FCSTD DOCUMENT  (FreeCAD 1.1R39176 (Git))
Label: hackrf2
License: All rights reserved
LicenseURL: https://en.wikipedia.org/wiki/All_rights_reserved
objects: Sketcher::SketchObject×1, PartDesign::Body×1
note: 3 computed .brp shape members not serialized (recipe doc carries the construction recipe); baked Part::Feature solids carry a one-line shape summary decoded from their .brp

FEATURE [Sketcher::SketchObject] Sketch
  ArcFitTolerance = 1e-06
  AttachmentSupport = -> [XY_Plane]
  FullyConstrained = false
  MakeInternals = false
  MapMode = 5
  sketch-geometry (26):
    g0: Circle CenterX=-8.35591 CenterY=25.54 CenterZ=0 NormalX=0 NormalY=0 NormalZ=1 AngleXU=0 Radius=1.65
    g1: Circle CenterX=58.7441 CenterY=25.54 CenterZ=0 NormalX=0 NormalY=0 NormalZ=1 AngleXU=0 Radius=1.65
    g2: LineSegment [constr] StartX=-92.1126 StartY=25.54 StartZ=0 EndX=115.727 EndY=25.54 EndZ=0
    g3: GeomPoint [constr] X=-10.0059 Y=25.54 Z=0
    g4: GeomPoint [constr] X=60.3941 Y=25.54 Z=0
    g5: Circle CenterX=19.1744 CenterY=-19.1627 CenterZ=0 NormalX=0 NormalY=0 NormalZ=1 AngleXU=0 Radius=1.65
    g6: Circle CenterX=58.7441 CenterY=-30.3 CenterZ=0 NormalX=0 NormalY=0 NormalZ=1 AngleXU=0 Radius=1.65
    g7: Circle CenterX=58.7441 CenterY=-92.13 CenterZ=0 NormalX=0 NormalY=0 NormalZ=1 AngleXU=0 Radius=1.65
    g8: Circle CenterX=55.1135 CenterY=37.367 CenterZ=0 NormalX=0 NormalY=0 NormalZ=1 AngleXU=0 Radius=1.65
    g9: Circle CenterX=-8.35591 CenterY=-92.13 CenterZ=0 NormalX=0 NormalY=0 NormalZ=1 AngleXU=0 Radius=1.65
    g10: GeomPoint [constr] X=-9.22115 Y=26.945 Z=0
    g11: GeomPoint [constr] X=20.0397 Y=-20.5676 Z=0
    g12: LineSegment [constr] StartX=-21.7434 StartY=47.2782 StartZ=0 EndX=29.3252 EndY=-35.645 EndZ=0
    g13: GeomPoint [constr] X=18.0808 Y=-20.3982 Z=0
    g14: LineSegment [constr] StartX=44.9983 StartY=10.0112 StartZ=0 EndX=-3.8972 EndY=-45.2271 EndZ=0
    g15: GeomPoint [constr] X=59.8377 Y=26.7755 Z=0
    g16: LineSegment [constr] StartX=58.7441 StartY=53.8008 StartZ=0 EndX=58.7441 EndY=-140.054 EndZ=0
    g17: GeomPoint [constr] X=58.7441 Y=23.89 Z=0
    g18: GeomPoint [constr] X=58.7441 Y=-28.65 Z=0
    g19: GeomPoint [constr] X=58.7441 Y=-93.78 Z=0
    g20: GeomPoint [constr] X=58.7441 Y=-28.65 Z=0
    g21: LineSegment [constr] StartX=131.191 StartY=-92.13 StartZ=0 EndX=-53.1494 EndY=-92.13 EndZ=0
    g22: LineSegment [constr] StartX=-8.35591 StartY=91.9074 StartZ=0 EndX=-8.35591 EndY=-151.657 EndZ=0
    g23: LineSegment [constr] StartX=-28.9239 StartY=-5.62487 StartZ=0 EndX=81.0484 EndY=-36.5777 EndZ=0
    g24: GeomPoint [constr] X=60.3324 Y=-30.747 Z=0
    g25: GeomPoint [constr] X=17.5861 Y=-18.7156 Z=0
  constraints (56):
    c: Diameter(g0) = 3.3
    c: Horizontal(g2)
    c: PointOnObject(g0,g2)
    c: PointOnObject(g1,g2)
    c: PointOnObject(g3,g2)
    c: PointOnObject(g3,g0)
    c: PointOnObject(g4,g2)
    c: PointOnObject(g4,g1)
    c: Equal(g1,g0)
    c: DistanceX(g3,g4) = 70.4
    c: Equal(g8,g0)
    c: Equal(g6,g0)
    c: Equal(g5,g0)
    c: Equal(g7,g0)
    c: Equal(g9,g0)
    c: PointOnObject(g0,g12)
    c: PointOnObject(g5,g12)
    c: PointOnObject(g11,g12)
    c: Distance(g11,g10) = 55.8
    c: PointOnObject(g13,g5)
    c: PointOnObject(g13,g14)
    c: PointOnObject(g5,g14)
    c: PointOnObject(g1,g14)
    c: PointOnObject(g15,g1)
    c: PointOnObject(g15,g14)
    c: Distance(g13,g15) = 63
    c: Vertical(g16)
    c: PointOnObject(g6,g16)
    c: PointOnObject(g1,g16)
    c: PointOnObject(g17,g1)
    c: PointOnObject(g17,g16)
    c: PointOnObject(g18,g6)
    c: PointOnObject(g18,g16)
    c: Distance(g18,g17) = 52.54
    c: PointOnObject(g7,g16)
    c: PointOnObject(g19,g7)
    c: PointOnObject(g19,g16)
    c: PointOnObject(g20,g6)
    c: PointOnObject(g20,g16)
    c: Distance(g19,g20) = 65.13
    c: Horizontal(g21)
    c: PointOnObject(g7,g21)
    c: PointOnObject(g9,g21)
    c: Vertical(g22)
    c: PointOnObject(g9,g22)
    c: PointOnObject(g0,g22)
    c: PointOnObject(g6,g23)
    c: PointOnObject(g5,g23)
    c: PointOnObject(g24,g23)
    c: PointOnObject(g24,g6)
    c: PointOnObject(g25,g23)
    c: PointOnObject(g25,g5)
    c: Distance(g25,g24) = 44.4072
    c: PointOnObject(g10,g0)
    c: PointOnObject(g10,g12)
    c: PointOnObject(g11,g5)
FEATURE [PartDesign::Body] Body
  AllowCompound = false
  Group = -> [Sketch]
  Origin = -> Origin
